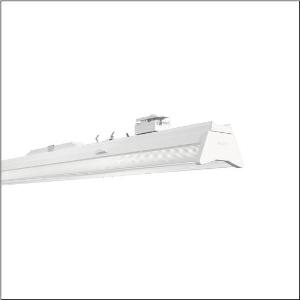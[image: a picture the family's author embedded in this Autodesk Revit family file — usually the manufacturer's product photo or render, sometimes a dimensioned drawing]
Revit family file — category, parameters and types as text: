
# Revit family: licross_r__21_performance_mo_52td16cn445g_c2c6
name_source: partatom
category: Lighting Fixtures
units: mm (PartAtom-declared; Revit-internal decimal feet)

## family parameters
Cut with Voids When Loaded = No
Host = Face
Light Source = No
Part Type = Normal
Room Calculation Point = No
Round Connector Dimension = Use Diameter
Shared = No

## types (1)
- --- (1 x LED, 4500 lm, 24.1 W, 4000K)
    Apparent Load = 24 VA
    CIE Flux Codes = 66 88 96 79 100
    Color Rendering = 80
    Color Temperature = 4000K
    Default Elevation = 1800 mm
    Description = Licross® 21 Performance MO, luminaire insert, of sheet steel, galvanised, coil coated, white, length: 1.500mm, width: 120mm, height: 123mm, LED rated luminous flux: 4.500lm, light colour: 840, control gear: ON/OFF Multilumen, CLOi, control gear: ECG Multilumen, with plug, 3-pole, with phase selection, mains connection: 220..240V, AC, 50/60Hz, start of lifetime: 24W, end of service life: 28W, halogen-free wiring, primary light control with lens, of plastic, primary optical cover: cover, of PMMA, CAT 2 (L<= 3000cd/m²), light emission: direct/indirect distribution, primary light characteristic: symmetric, protection rating (complete): IP54, insulation class (complete): insulation class I (protective earthing), certification: CE, ENEC, UKCA, protection symbol: D if used in an environment with non-conductive dust loads with corresponding accessories, impact resistance: IK06, permissible ambient temperature for indoor applications: -35..+55°C, corresponds to IFS (International Featured Standards) requirements for safety and quality in the food industry, reducing of maximum allowable ambient temperature of 5°C with ceiling mounting, LABS conformity tested according to VDMA 24364:2018-05, packaging unit: 1 piece
    Height = 114 mm
    Lamp = 1 x LED
    Lamp Light Flux = 4500 lm
    Lamp Power = 24.1 W
    Lamp count = 1
    Length = 1500 mm
    Luminous efficacy = 187 lm/W
    Manufacturer = Siteco
    ModVariant = No
    Model = 52TD16CN445G
    Mounting Place = Ceiling
    Mounting Type = Pendant
    Number of Poles = 1
    OnlyDefault = Yes
    Power Factor = 1
    Product Name = Licross® 21 Performance MO
    Product group = luminaire insert
    ProductGroupID = 901
    Protection Class = Protection class I
    Protection Degree = IP 54
    RLX_Detail_Level = 1
    RLX_Emergency_Light_Flux = 0 lm
    RLX_Emergency_Type = 0
    RLX_Emergency_Type_DB = No
    RlxData = <blob elided: 31465 chars, md5=963a6aeb>
    Socket = socket
    Standby Power = 0 W
    System Light Flux = 4500 lm
    System Power = 24 W
    Type Comments = factory setting: luminous flux: 100 % | (A | C | E) | 55 mA
    Type Image = l_1256138.jpg
    URL = http://relux.com
    VarID = @adj_000173
    Voltage = 0 V
    Weight = 0.00 kg
    Width = 120 mm

## geometry (parser evidence)
native form markers: Blend x4, Sweep x11
no freeform markers — native parametric forms only
